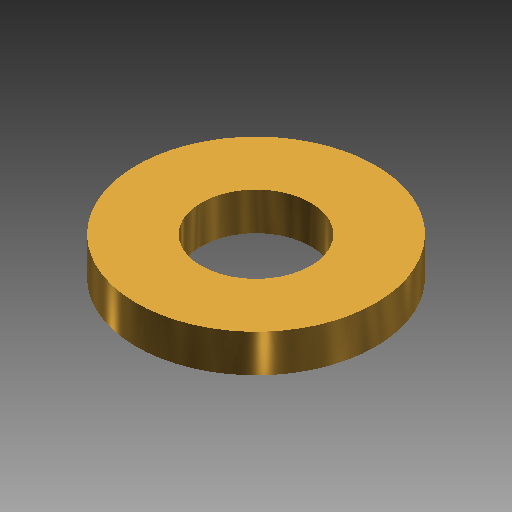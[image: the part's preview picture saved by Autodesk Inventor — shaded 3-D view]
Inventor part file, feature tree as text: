
AUTODESK INVENTOR PART (.ipt)
format: ipt  version: 2019 (Build 230136000, 136)  size: 96,256 bytes
history: native  units: mm
features: revolve x1, sketch x1
ambient origin geometry x8: Origin, YZ Plane, XZ Plane, XY Plane, X Axis, Y Axis, Z Axis, Center Point
bodies: Solid1 (feature_tree)
feature tree (2):
  revolve  "Revolution1"  [1 undecoded]
  sketch  "Sketch1"  dims[d0=8.7mm d1=19.0mm d2=3.0mm d3=90.0deg]
note: 1 required parameter value undecoded (feature->parameter linkage not recoverable at this tier; creation-order binding heuristic only, values carry confidence <= 0.55)
